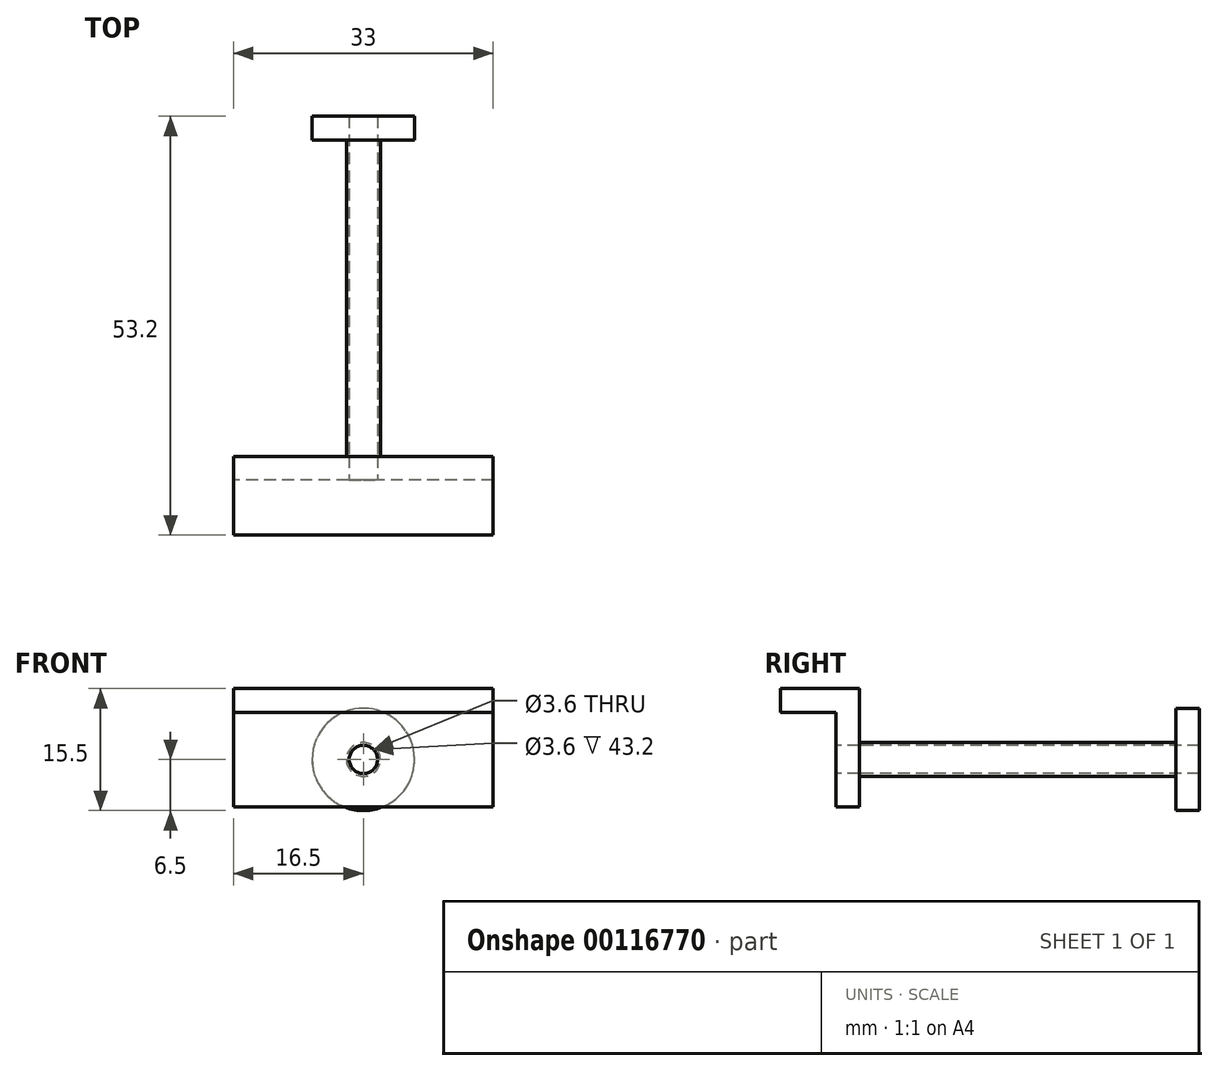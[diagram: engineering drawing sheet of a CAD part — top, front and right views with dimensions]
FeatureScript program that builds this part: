
annotation { "Feature Type Name" : "Feature", "Feature Type Description" : "" }
export const myFeature = defineFeature(function(context is Context, id is Id, definition is map)
    precondition{}
    {
        {
            var Q0;
            Q0=qCreatedBy(makeId("Front.planeOp"),FACE);
            var sketch = newSketch(context, id + "F0", { "sketchPlane" : qUnion([Q0])});
            skCircle(sketch, "E0", {"center": v(0, 0) * mm, "radius": 6.5 * mm});
            skSolve(sketch);
        }
        {
            var Q0;
            Q0=qSketchRegion(id+"F0",true);
            extrude(context, id + "F1", {"entities" : qUnion([Q0]), "depth" : 3 * mm});
        }
        {
            var Q0;
            Q0=makeQuery(id+"F1.opExtrude","CAP_FACE",FACE,{"disambiguationData":[OSD([sQuery(id+"F0.wireOp",EDGE,"E0")])],"isStart":false});
            var sketch = newSketch(context, id + "F2", { "sketchPlane" : qUnion([Q0])});
            skCircle(sketch, "E1", {"center": v(0, 0) * mm, "radius": 2.15 * mm});
            skSolve(sketch);
        }
        {
            var Q0;
            Q0=qSketchRegion(id+"F2",true);
            extrude(context, id + "F3", {"entities" : qUnion([Q0]), "operationType" : NewBodyOperationType.ADD, "depth" : 40.2 * mm});
        }
        {
            var Q0;
            Q0=makeQuery(id+"F3.opExtrude","CAP_FACE",FACE,{"disambiguationData":[OSD([sQuery(id+"F2.wireOp",EDGE,"E1")])],"isStart":false});
            var sketch = newSketch(context, id + "F4", { "sketchPlane" : qUnion([Q0])});
            skCircle(sketch, "E2", {"center": v(0, 0) * mm, "radius": 1.8 * mm});
            skSolve(sketch);
        }
        {
            var Q0;
            Q0=qSketchRegion(id+"F4",true);
            extrude(context, id + "F5", {"entities" : qUnion([Q0]), "operationType" : NewBodyOperationType.REMOVE, "oppositeDirection" : true, "depth" : 12 * mm});
        }
        {
            var Q0;
            Q0=makeQuery(id+"F3.opExtrude","CAP_FACE",FACE,{"disambiguationData":[OSD([sQuery(id+"F2.wireOp",EDGE,"E1")])],"isStart":false});
            var sketch = newSketch(context, id + "F6", { "sketchPlane" : qUnion([Q0])});
            skLineSegment(sketch, "E3.bottom", {"start": v(16.5, 6) * mm, "end": v(-16.5, 6) * mm});
            skLineSegment(sketch, "E3.top", {"start": v(16.5, -6) * mm, "end": v(-16.5, -6) * mm});
            skLineSegment(sketch, "E3.left", {"start": v(16.5, 6) * mm, "end": v(16.5, -6) * mm});
            skLineSegment(sketch, "E3.right", {"start": v(-16.5, 6) * mm, "end": v(-16.5, -6) * mm});
            skPoint(sketch, "E3.middle", {"position": v(0, 0) * mm});
            skSolve(sketch);
        }
        {
            var Q0;
            Q0=qSketchRegion(id+"F6",true);
            extrude(context, id + "F7", {"entities" : qUnion([Q0]), "depth" : 3 * mm});
        }
        {
            var Q0;
            Q0=makeQuery(id+"F7.opExtrude","SWEPT_FACE",FACE,{"disambiguationData":[OSD([sQuery(id+"F6.wireOp",EDGE,"E3.bottom")])]});
            var sketch = newSketch(context, id + "F8", { "sketchPlane" : qUnion([Q0])});
            skLineSegment(sketch, "E4.bottom", {"start": v(-16.5, -43.2) * mm, "end": v(16.5, -43.2) * mm});
            skLineSegment(sketch, "E4.top", {"start": v(-16.5, -53.2) * mm, "end": v(16.5, -53.2) * mm});
            skLineSegment(sketch, "E4.left", {"start": v(-16.5, -43.2) * mm, "end": v(-16.5, -53.2) * mm});
            skLineSegment(sketch, "E4.right", {"start": v(16.5, -43.2) * mm, "end": v(16.5, -53.2) * mm});
            skSolve(sketch);
        }
        {
            var Q0;
            Q0=qSketchRegion(id+"F8",true);
            extrude(context, id + "F9", {"entities" : qUnion([Q0]), "operationType" : NewBodyOperationType.ADD, "depth" : 3 * mm});
        }
        {
            var Q0;
            Q0=makeQuery(id+"F7.opExtrude","CAP_FACE",FACE,{"disambiguationData":[OSD([sQuery(id+"F6.wireOp",EDGE,"E3.bottom"),sQuery(id+"F6.wireOp",EDGE,"E3.top"),sQuery(id+"F6.wireOp",EDGE,"E3.left"),sQuery(id+"F6.wireOp",EDGE,"E3.right")])],"isStart":false});
            var sketch = newSketch(context, id + "F10", { "sketchPlane" : qUnion([Q0])});
            skCircle(sketch, "E5", {"center": v(0, 0) * mm, "radius": 1.8 * mm});
            skSolve(sketch);
        }
        {
            var Q0;
            Q0=qSketchRegion(id+"F10",true);
            extrude(context, id + "F11", {"entities" : qUnion([Q0]), "operationType" : NewBodyOperationType.REMOVE, "endBound" : BoundingType.THROUGH_ALL, "oppositeDirection" : true, "depth" : 25 * mm});
        }
    });
